# Revit family: Electrical_Controls_Conspec_Optio-V-CO-NO2-Detector
name_source: partatom
category: Electrical Fixtures
units: mm (PartAtom-declared; Revit-internal decimal feet)

## family parameters
Classification Number = 23.85.30.21
Cut with Voids When Loaded = No
Host = Face
Maintain Annotation Orientation = No
Part Type = Normal
Room Calculation Point = No
Round Connector Dimension = Use Diameter
Shared = No

## types (1)
- OPTIO V - CO and NO2 - 12V-24V DC
    Alarm = 4 Alarms with hysteresis and hold times, sensor Fail-High and Fail-Low
    Apparent Load = 0 VA
    Assembly Code = D5030
    Date Updated = 2023/10/17
    Default Elevation = 0 "
    Depth = 3.94 "
    Description = OPTIO V - CO and NO2 Detector for ventilation control in enclosed parking areas
    Display = Intuitive menu navigation via LCD
    Enclosure Rating and Finish = NEMA 4X
    Frequency = 0 Hz
    Height = 9.15 "
    Input/Output = 6 Digital I/O (0-0.5V), 6 Relay Ports (250VAC-220VDC. 2A), 2channels 4-20mA outputs
    Keynote = 16000
    Manufacturer = CONSPEC Controls
    Maximum Current Consumption = 50 mA
    Model = OPTIO V - CO and NO2 - 12V-24V DC
    Number of Poles = 3
    Operating Humidity = 15% to 90% RH Non-Condesing
    Operating Temperature = -4°F to +122°F
    Power Factor = 0.8
    Product Material = Conspec - Plastic - FR ABS - Grey
    Product data url = https://bimobject.com
    Sensor Life Expectancy = 7 years for CO and 2 years for NO2
    Sensor Range = 0-500ppm for CO and 0-20ppm for NO2
    URL = https://www.conspec-controls.com
    Version = 1
    Voltage = 24 V
    Voltage Range = 12V-24V DC
    Weight = 0.00 lbf
    Width = 6.98 "
    z_DC = Yes

## geometry (parser evidence)
native form markers: Sweep x4
no freeform markers — native parametric forms only
